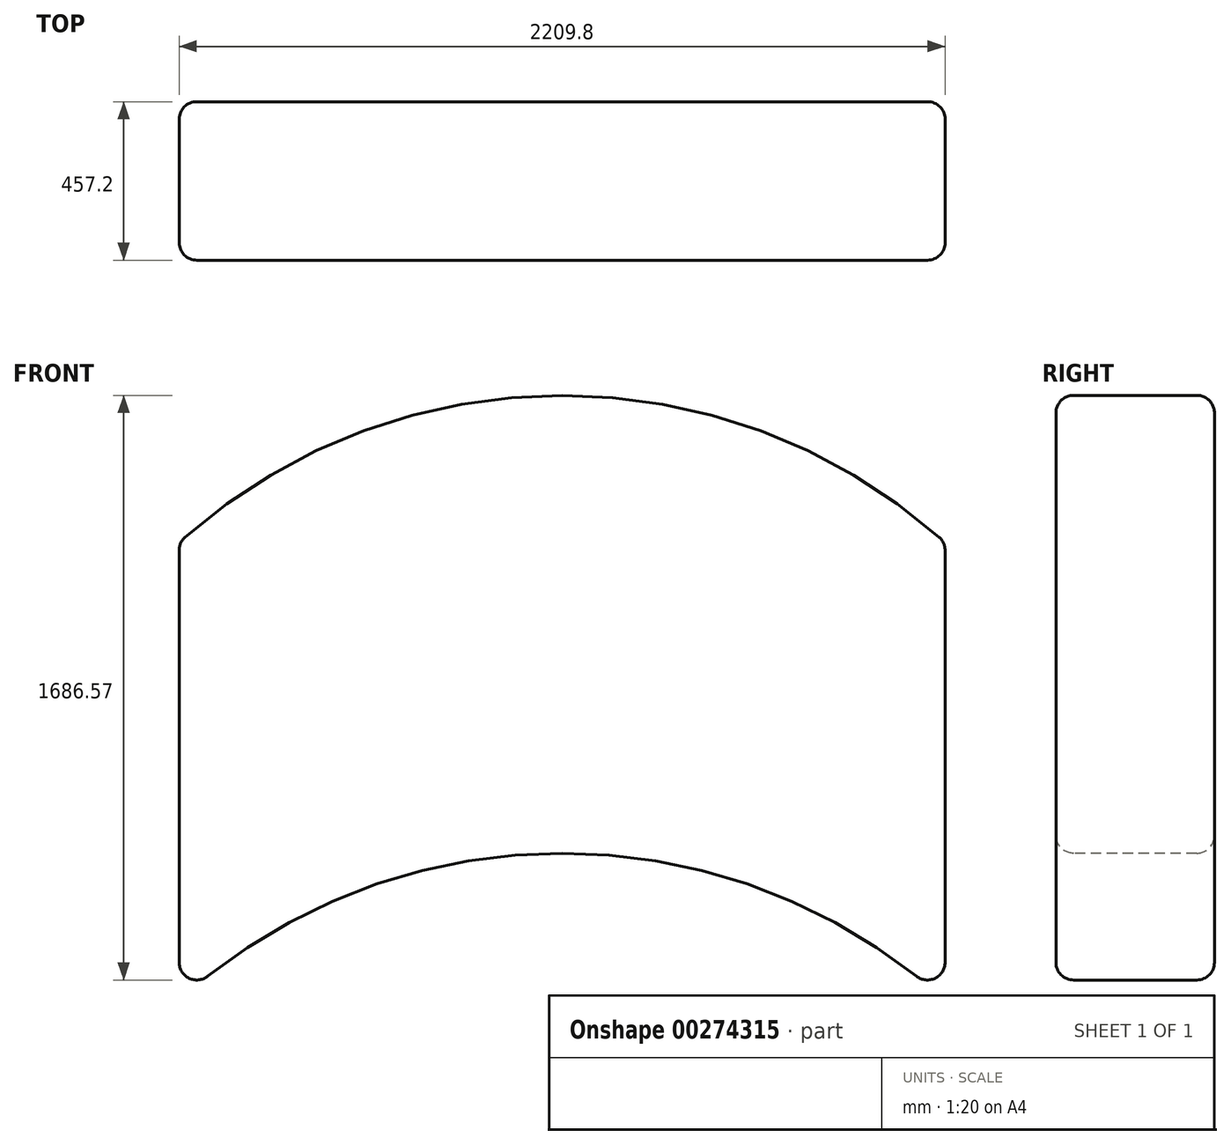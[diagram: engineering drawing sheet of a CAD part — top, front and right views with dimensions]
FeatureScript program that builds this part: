
annotation { "Feature Type Name" : "Feature", "Feature Type Description" : "" }
export const myFeature = defineFeature(function(context is Context, id is Id, definition is map)
    precondition{}
    {
        {
            var Q0;
            Q0=qCreatedBy(makeId("Front.planeOp"),FACE);
            var sketch = newSketch(context, id + "F0", { "sketchPlane" : qUnion([Q0])});
            skArc(sketch, "E0", {"start": v(1104.9, 0) * mm, "mid": v(0, 424.22) * mm, "end": v(-1104.9, 0) * mm});
            skLineSegment(sketch, "E1", {"start": v(1104.9, 0) * mm, "end": v(1104.9, 1320.8) * mm});
            skLineSegment(sketch, "E2", {"start": v(-1104.9, 0) * mm, "end": v(-1104.9, 1320.8) * mm});
            skArc(sketch, "E3", {"start": v(1104.9, 1320.8) * mm, "mid": v(0, 1745.02) * mm, "end": v(-1104.9, 1320.8) * mm});
            skSolve(sketch);
        }
        {
            var Q0;
            Q0=makeQuery(id+"F0.imprint","IMPRINT",FACE,{"disambiguationData":[TD([[makeQuery(id+"F0.imprint","IMPRINT",EDGE,{"derivedFrom":sQuery(id+"F0.wireOp",EDGE,"E0")}),-1.0]])]});
            extrude(context, id + "F1", {"entities" : qUnion([Q0]), "oppositeDirection" : true, "depth" : 457.2 * mm});
        }
        {
            var Q0;
            Q0=makeQuery(id+"F1.opExtrude","CAP_EDGE",EDGE,{"disambiguationData":[OSD([sQuery(id+"F0.wireOp",EDGE,"E1")])],"isStart":true});
            var Q1;
            Q1=makeQuery(id+"F1.opExtrude","CAP_EDGE",EDGE,{"disambiguationData":[OSD([sQuery(id+"F0.wireOp",EDGE,"E3")])],"isStart":true});
            var Q2;
            Q2=makeQuery(id+"F1.opExtrude","CAP_EDGE",EDGE,{"disambiguationData":[OSD([sQuery(id+"F0.wireOp",EDGE,"E2")])],"isStart":true});
            var Q3;
            Q3=makeQuery(id+"F1.opExtrude","SWEPT_EDGE",EDGE,{"disambiguationData":[OSD([sQuery(id+"F0.wireOp",EDGE,"E1"),sQuery(id+"F0.wireOp",EDGE,"E3")])]});
            var Q4;
            Q4=makeQuery(id+"F1.opExtrude","CAP_EDGE",EDGE,{"disambiguationData":[OSD([sQuery(id+"F0.wireOp",EDGE,"E3")])],"isStart":false});
            var Q5;
            Q5=makeQuery(id+"F1.opExtrude","SWEPT_EDGE",EDGE,{"disambiguationData":[OSD([sQuery(id+"F0.wireOp",EDGE,"E2"),sQuery(id+"F0.wireOp",EDGE,"E3")])]});
            var Q6;
            Q6=makeQuery(id+"F1.opExtrude","SWEPT_EDGE",EDGE,{"disambiguationData":[OSD([sQuery(id+"F0.wireOp",EDGE,"E0"),sQuery(id+"F0.wireOp",EDGE,"E1")])]});
            var Q7;
            Q7=makeQuery(id+"F1.opExtrude","SWEPT_EDGE",EDGE,{"disambiguationData":[OSD([sQuery(id+"F0.wireOp",EDGE,"E0"),sQuery(id+"F0.wireOp",EDGE,"E2")])]});
            var Q8;
            Q8=makeQuery(id+"F1.opExtrude","CAP_EDGE",EDGE,{"disambiguationData":[OSD([sQuery(id+"F0.wireOp",EDGE,"E0")])],"isStart":true});
            var Q9;
            Q9=makeQuery(id+"F1.opExtrude","CAP_EDGE",EDGE,{"disambiguationData":[OSD([sQuery(id+"F0.wireOp",EDGE,"E0")])],"isStart":false});
            var Q10;
            Q10=makeQuery(id+"F1.opExtrude","CAP_EDGE",EDGE,{"disambiguationData":[OSD([sQuery(id+"F0.wireOp",EDGE,"E1")])],"isStart":false});
            var Q11;
            Q11=makeQuery(id+"F1.opExtrude","CAP_EDGE",EDGE,{"disambiguationData":[OSD([sQuery(id+"F0.wireOp",EDGE,"E2")])],"isStart":false});
            fillet(context, id + "F2", {"entities" : qUnion([Q0, Q1, Q2, Q3, Q4, Q5, Q6, Q7, Q8, Q9, Q10, Q11]), "radius" : 50.8 * mm, "tangentPropagation" : true, "allowEdgeOverflow" : false});
        }
    });
